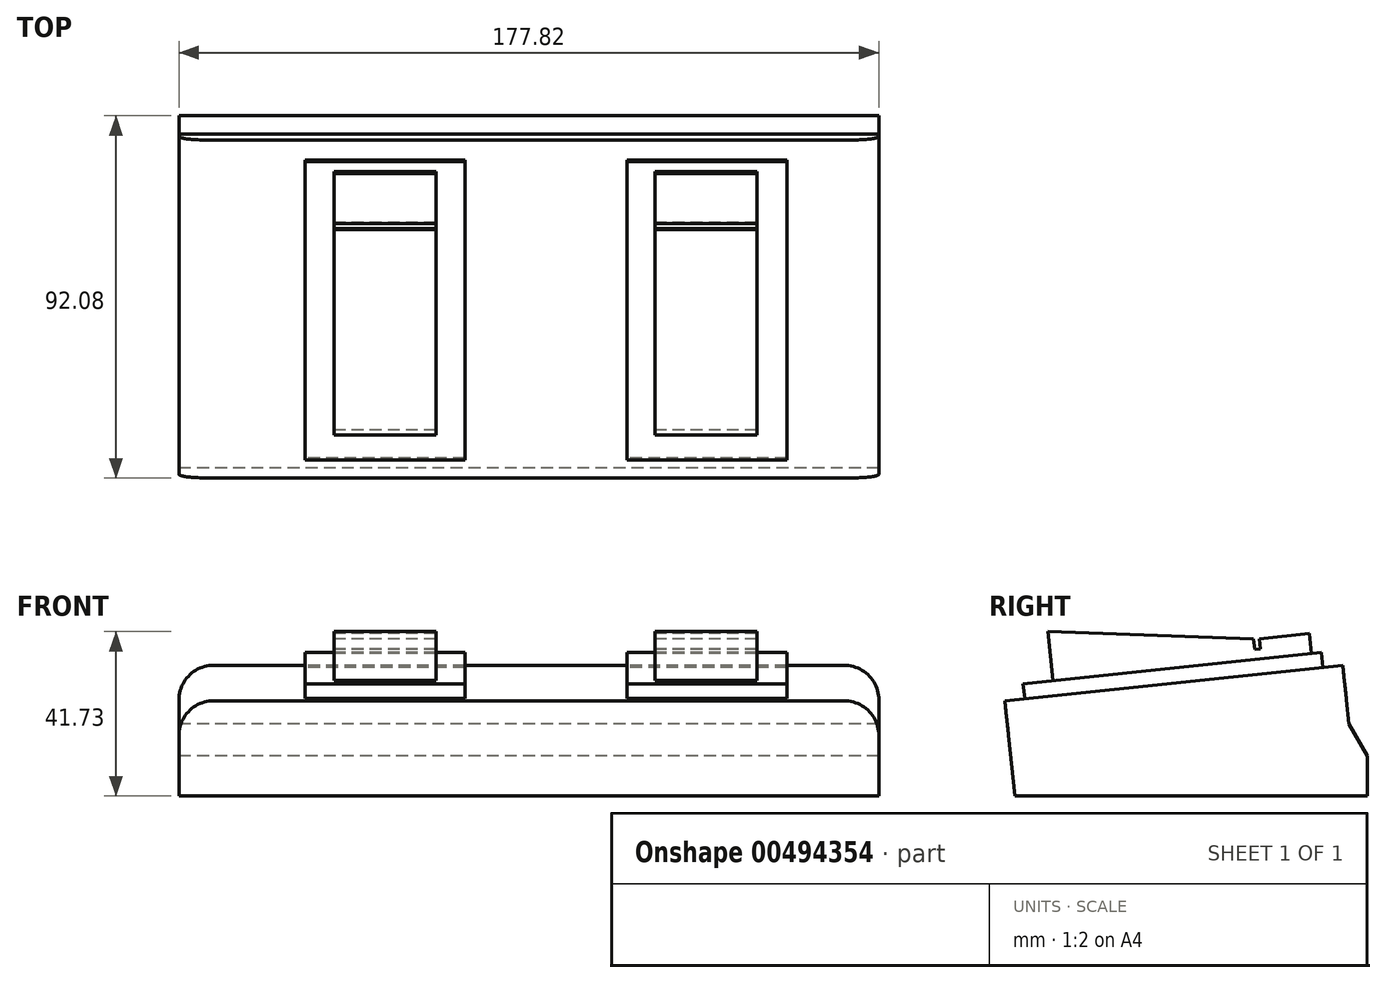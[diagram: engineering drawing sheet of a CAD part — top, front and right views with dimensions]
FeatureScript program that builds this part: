
annotation { "Feature Type Name" : "Feature", "Feature Type Description" : "" }
export const myFeature = defineFeature(function(context is Context, id is Id, definition is map)
    precondition{}
    {
        {
            var Q0;
            Q0=qCreatedBy(makeId("Right.planeOp"),FACE);
            var sketch = newSketch(context, id + "F0", { "sketchPlane" : qUnion([Q0])});
            skLineSegment(sketch, "E0", {"start": v(2.54, 0) * mm, "end": v(92.08, 0) * mm});
            skLineSegment(sketch, "E1", {"start": v(92.08, 0) * mm, "end": v(92.08, 10.16) * mm});
            skLineSegment(sketch, "E2", {"start": v(92.08, 10.16) * mm, "end": v(87.43, 18.21) * mm});
            skLineSegment(sketch, "E3", {"start": v(87.43, 18.21) * mm, "end": v(85.85, 33.19) * mm});
            skLineSegment(sketch, "E4", {"start": v(85.85, 33.19) * mm, "end": v(0, 24.17) * mm});
            skLineSegment(sketch, "E5", {"start": v(0, 24.17) * mm, "end": v(2.54, 0) * mm});
            skLineSegment(sketch, "E6", {"start": v(80.8, 32.66) * mm, "end": v(80.4, 36.45) * mm});
            skLineSegment(sketch, "E7", {"start": v(80.4, 36.45) * mm, "end": v(4.65, 28.49) * mm});
            skLineSegment(sketch, "E8", {"start": v(4.65, 28.49) * mm, "end": v(5.05, 24.7) * mm});
            skLineSegment(sketch, "E9", {"start": v(77.87, 36.18) * mm, "end": v(77.34, 41.23) * mm});
            skLineSegment(sketch, "E10", {"start": v(77.34, 41.23) * mm, "end": v(64.71, 39.9) * mm});
            skLineSegment(sketch, "E11", {"start": v(64.71, 39.9) * mm, "end": v(64.98, 37.38) * mm});
            skLineSegment(sketch, "E12", {"start": v(64.98, 37.38) * mm, "end": v(63.46, 37.22) * mm});
            skLineSegment(sketch, "E13", {"start": v(63.46, 37.22) * mm, "end": v(63.18, 39.9) * mm});
            skLineSegment(sketch, "E14", {"start": v(63.18, 39.9) * mm, "end": v(10.92, 41.73) * mm});
            skLineSegment(sketch, "E15", {"start": v(10.92, 41.73) * mm, "end": v(12.23, 29.28) * mm});
            skSolve(sketch);
        }
        {
            var Q0;
            Q0=makeQuery(id+"F0.imprint","IMPRINT",FACE,{"disambiguationData":[TD([[makeQuery(id+"F0.imprint","IMPRINT",EDGE,{"derivedFrom":sQuery(id+"F0.wireOp",EDGE,"E0")}),1.0]])]});
            extrude(context, id + "F1", {"entities" : qUnion([Q0]), "depth" : 177.8 * mm + 7 / 406.4 * mm});
        }
        {
            var Q0;
            {var subQ1=sQuery(id+"F0.wireOp",EDGE,"E6");Q0=makeQuery(id+"F0.imprint","IMPRINT",FACE,{"disambiguationData":[TD([[makeQuery(id+"F0.imprint","IMPRINT",EDGE,{"derivedFrom":subQ1}),1.0]])]});}
            extrude(context, id + "F2", {"entities" : qUnion([Q0]), "depth" : 40.64 * mm});
        }
        {
            var Q0;
            Q0=makeQuery(id+"F2.opExtrude","SWEPT_BODY",BODY,{"disambiguationData":[OSD([sQuery(id+"F0.wireOp",EDGE,"E4"),sQuery(id+"F0.wireOp",EDGE,"E6"),sQuery(id+"F0.wireOp",EDGE,"E7"),sQuery(id+"F0.wireOp",EDGE,"E8")])]});
            transform(context, id + "F3", {"entities" : qUnion([Q0]), "transformType" : TransformType.TRANSLATION_3D, "dx" : 32 * mm, "dy" : 0 * mm, "dz" : 0 * mm, "makeCopy" : false});
        }
        {
            var Q0;
            Q0=makeQuery(id+"F2.opExtrude","SWEPT_BODY",BODY,{"disambiguationData":[OSD([sQuery(id+"F0.wireOp",EDGE,"E4"),sQuery(id+"F0.wireOp",EDGE,"E6"),sQuery(id+"F0.wireOp",EDGE,"E7"),sQuery(id+"F0.wireOp",EDGE,"E8")])]});
            transform(context, id + "F4", {"entities" : qUnion([Q0]), "transformType" : TransformType.TRANSLATION_3D, "dx" : 81.8 * mm, "dy" : 0 * mm, "dz" : 0 * mm, "makeCopy" : true});
        }
        {
            var Q0;
            {var subQ0=sQuery(id+"F0.wireOp",EDGE,"E9");Q0=makeQuery(id+"F0.imprint","IMPRINT",FACE,{"disambiguationData":[TD([[makeQuery(id+"F0.imprint","IMPRINT",EDGE,{"derivedFrom":subQ0}),1.0]])]});}
            extrude(context, id + "F5", {"entities" : qUnion([Q0]), "depth" : 25.9 * mm});
        }
        {
            var Q0;
            Q0=makeQuery(id+"F5.opExtrude","SWEPT_BODY",BODY,{"disambiguationData":[OSD([sQuery(id+"F0.wireOp",EDGE,"E7"),sQuery(id+"F0.wireOp",EDGE,"E9"),sQuery(id+"F0.wireOp",EDGE,"E10"),sQuery(id+"F0.wireOp",EDGE,"E11"),sQuery(id+"F0.wireOp",EDGE,"E12"),sQuery(id+"F0.wireOp",EDGE,"E13"),sQuery(id+"F0.wireOp",EDGE,"E14"),sQuery(id+"F0.wireOp",EDGE,"E15")])]});
            transform(context, id + "F6", {"entities" : qUnion([Q0]), "transformType" : TransformType.TRANSLATION_3D, "dx" : 39.37 * mm, "dy" : 0 * mm, "dz" : 0 * mm, "makeCopy" : false});
        }
        {
            var Q0;
            Q0=makeQuery(id+"F5.opExtrude","SWEPT_BODY",BODY,{"disambiguationData":[OSD([sQuery(id+"F0.wireOp",EDGE,"E7"),sQuery(id+"F0.wireOp",EDGE,"E9"),sQuery(id+"F0.wireOp",EDGE,"E10"),sQuery(id+"F0.wireOp",EDGE,"E11"),sQuery(id+"F0.wireOp",EDGE,"E12"),sQuery(id+"F0.wireOp",EDGE,"E13"),sQuery(id+"F0.wireOp",EDGE,"E14"),sQuery(id+"F0.wireOp",EDGE,"E15")])]});
            transform(context, id + "F7", {"entities" : qUnion([Q0]), "transformType" : TransformType.TRANSLATION_3D, "dx" : 81.53 * mm, "dy" : 0 * mm, "dz" : 0 * mm, "makeCopy" : true});
        }
        {
            var Q0;
            Q0=makeQuery(id+"F1.opExtrude","CAP_EDGE",EDGE,{"disambiguationData":[OSD([sQuery(id+"F0.wireOp",EDGE,"E4")])],"isStart":true});
            var Q1;
            Q1=makeQuery(id+"F1.opExtrude","CAP_EDGE",EDGE,{"disambiguationData":[OSD([sQuery(id+"F0.wireOp",EDGE,"E4")])],"isStart":false});
            fillet(context, id + "F8", {"entities" : qUnion([Q0, Q1]), "radius" : 8.9 * mm, "tangentPropagation" : true, "allowEdgeOverflow" : false});
        }
    });
